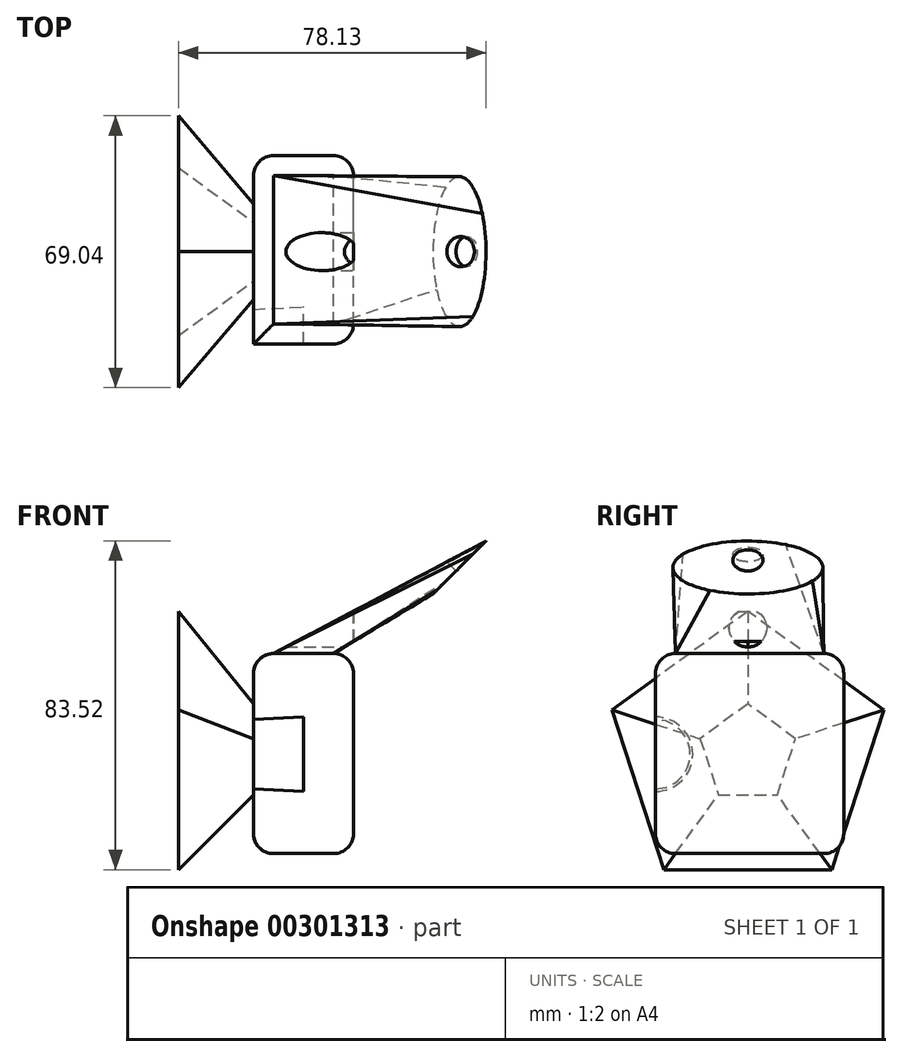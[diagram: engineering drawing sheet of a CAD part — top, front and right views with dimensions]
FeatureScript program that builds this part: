
annotation { "Feature Type Name" : "Feature", "Feature Type Description" : "" }
export const myFeature = defineFeature(function(context is Context, id is Id, definition is map)
    precondition{}
    {
        {
            var Q0;
            Q0=qCreatedBy(makeId("Right.planeOp"),FACE);
            var sketch = newSketch(context, id + "F0", { "sketchPlane" : qUnion([Q0])});
            skLineSegment(sketch, "E0.bottom", {"start": v(-23.46, 25.57) * mm, "end": v(24.36, 25.57) * mm});
            skLineSegment(sketch, "E0.top", {"start": v(-23.46, -25.27) * mm, "end": v(24.36, -25.27) * mm});
            skLineSegment(sketch, "E0.left", {"start": v(-23.46, 25.57) * mm, "end": v(-23.46, -25.27) * mm});
            skLineSegment(sketch, "E0.right", {"start": v(24.36, 25.57) * mm, "end": v(24.36, -25.27) * mm});
            skSolve(sketch);
        }
        {
            var Q0;
            Q0=makeQuery(id+"F0.imprint","IMPRINT",FACE,{"disambiguationData":[TD([[makeQuery(id+"F0.imprint","IMPRINT",EDGE,{"derivedFrom":sQuery(id+"F0.wireOp",EDGE,"E0.bottom")}),-1.0]])]});
            extrude(context, id + "F1", {"entities" : qUnion([Q0]), "depth" : 25.4 * mm});
        }
        {
            var Q0;
            Q0=makeQuery(id+"F1.opExtrude","SWEPT_EDGE",EDGE,{"disambiguationData":[OSD([sQuery(id+"F0.wireOp",EDGE,"E0.bottom"),sQuery(id+"F0.wireOp",EDGE,"E0.left")])]});
            var Q1;
            Q1=makeQuery(id+"F1.opExtrude","SWEPT_EDGE",EDGE,{"disambiguationData":[OSD([sQuery(id+"F0.wireOp",EDGE,"E0.bottom"),sQuery(id+"F0.wireOp",EDGE,"E0.right")])]});
            var Q2;
            Q2=makeQuery(id+"F1.opExtrude","SWEPT_FACE",FACE,{"disambiguationData":[OSD([sQuery(id+"F0.wireOp",EDGE,"E0.bottom")])]});
            var Q3;
            Q3=makeQuery(id+"F1.opExtrude","CAP_FACE",FACE,{"disambiguationData":[OSD([sQuery(id+"F0.wireOp",EDGE,"E0.bottom"),sQuery(id+"F0.wireOp",EDGE,"E0.top"),sQuery(id+"F0.wireOp",EDGE,"E0.left"),sQuery(id+"F0.wireOp",EDGE,"E0.right")])],"isStart":false});
            var Q4;
            Q4=makeQuery(id+"F1.opExtrude","CAP_EDGE",EDGE,{"disambiguationData":[OSD([sQuery(id+"F0.wireOp",EDGE,"E0.right")])],"isStart":true});
            var Q5;
            Q5=makeQuery(id+"F1.opExtrude","SWEPT_EDGE",EDGE,{"disambiguationData":[OSD([sQuery(id+"F0.wireOp",EDGE,"E0.top"),sQuery(id+"F0.wireOp",EDGE,"E0.right")])]});
            var Q6;
            Q6=makeQuery(id+"F1.opExtrude","CAP_EDGE",EDGE,{"disambiguationData":[OSD([sQuery(id+"F0.wireOp",EDGE,"E0.top")])],"isStart":true});
            var Q7;
            Q7=makeQuery(id+"F1.opExtrude","SWEPT_EDGE",EDGE,{"disambiguationData":[OSD([sQuery(id+"F0.wireOp",EDGE,"E0.top"),sQuery(id+"F0.wireOp",EDGE,"E0.left")])]});
            fillet(context, id + "F2", {"entities" : qUnion([Q0, Q1, Q2, Q3, Q4, Q5, Q6, Q7]), "radius" : 5.08 * mm, "tangentPropagation" : true, "allowEdgeOverflow" : false});
        }
        {
            var Q0;
            {var subQ0=sQuery(id+"F0.wireOp",EDGE,"E0.bottom");Q0=makeQuery(id+"F2.opFillet","BLEND_EDGE",EDGE,{"blendedFrom":[makeQuery(id+"F1.opExtrude","CAP_EDGE",EDGE,{"disambiguationData":[OSD([subQ0])],"isStart":false}),makeQuery(id+"F1.opExtrude","CAP_FACE",FACE,{"disambiguationData":[OSD([subQ0,sQuery(id+"F0.wireOp",EDGE,"E0.top"),sQuery(id+"F0.wireOp",EDGE,"E0.left"),sQuery(id+"F0.wireOp",EDGE,"E0.right")])],"isStart":false})],"blendedInto":[makeQuery(id+"F1.opExtrude","CAP_FACE",FACE,{"disambiguationData":[OSD([subQ0,sQuery(id+"F0.wireOp",EDGE,"E0.top"),sQuery(id+"F0.wireOp",EDGE,"E0.left"),sQuery(id+"F0.wireOp",EDGE,"E0.right")])],"isStart":false})]});}
            var Q1;
            Q1=makeQuery(id+"F1.opExtrude","CAP_FACE",FACE,{"disambiguationData":[OSD([sQuery(id+"F0.wireOp",EDGE,"E0.bottom"),sQuery(id+"F0.wireOp",EDGE,"E0.top"),sQuery(id+"F0.wireOp",EDGE,"E0.left"),sQuery(id+"F0.wireOp",EDGE,"E0.right")])],"isStart":false});
            cPlane(context, id + "F3", {"entities" : qUnion([Q0, Q1]), "cplaneType" : CPlaneType.LINE_ANGLE, "offset" : 25.4 * mm, "angle" : 45 * degree, "width" : 152.4 * mm, "height" : 152.4 * mm});
        }
        {
            var Q0;
            Q0=qCreatedBy(id+"F3.planeOp",FACE);
            var sketch = newSketch(context, id + "F4", { "sketchPlane" : qUnion([Q0])});
            skEllipse(sketch, "E1", {"center": v(0, 70.55) * mm, "majorRadius": 19.05 * mm, "minorRadius": 9.53 * mm, "majorAxis": v(1, 0)});
            skSolve(sketch);
        }
        {
            var Q1;
            Q1=makeQuery(id+"F1.opExtrude","SWEPT_FACE",FACE,{"disambiguationData":[OSD([sQuery(id+"F0.wireOp",EDGE,"E0.bottom")])]});
            var Q2;
            Q2=makeQuery(id+"F4.imprint","IMPRINT",FACE,{"disambiguationData":[TD([[makeQuery(id+"F4.imprint","IMPRINT",EDGE,{"derivedFrom":sQuery(id+"F4.wireOp",EDGE,"E1")}),1.0]])]});
            loft(context, id + "F5", {"operationType" : NewBodyOperationType.ADD, "sheetProfilesArray" : [{ "sheetProfileEntities" : qUnion([Q1]) }, { "sheetProfileEntities" : qUnion([Q2]) }]});
        }
        {
            var Q0;
            Q0=makeQuery(id+"F1.opExtrude","CAP_FACE",FACE,{"disambiguationData":[OSD([sQuery(id+"F0.wireOp",EDGE,"E0.bottom"),sQuery(id+"F0.wireOp",EDGE,"E0.top"),sQuery(id+"F0.wireOp",EDGE,"E0.left"),sQuery(id+"F0.wireOp",EDGE,"E0.right")])],"isStart":false});
            var sketch = newSketch(context, id + "F6", { "sketchPlane" : qUnion([Q0])});
            skCircle(sketch, "E2", {"center": v(0, 32.05) * mm, "radius": 4.81 * mm});
            skSolve(sketch);
        }
        {
            var Q0;
            Q0 = qSketchRegion(id + "F6", true);
            extrude(context, id + "F7", {"entities" : qUnion([Q0]), "operationType" : NewBodyOperationType.REMOVE, "endBound" : BoundingType.THROUGH_ALL, "oppositeDirection" : true, "depth" : 25.4 * mm});
        }
        {
            var Q0;
            Q0=makeQuery(id+"F1.opExtrude","CAP_FACE",FACE,{"disambiguationData":[OSD([sQuery(id+"F0.wireOp",EDGE,"E0.bottom"),sQuery(id+"F0.wireOp",EDGE,"E0.top"),sQuery(id+"F0.wireOp",EDGE,"E0.left"),sQuery(id+"F0.wireOp",EDGE,"E0.right")])],"isStart":true});
            var sketch = newSketch(context, id + "F8", { "sketchPlane" : qUnion([Q0])});
            skCircle(sketch, "E3", {"center": v(23.46, 0) * mm, "radius": 8.79 * mm});
            skSolve(sketch);
        }
        {
            var Q0;
            {var subQ0=sQuery(id+"F8.wireOp",EDGE,"E3");var subQ1=makeQuery(id+"F1.opExtrude","CAP_EDGE",EDGE,{"disambiguationData":[OSD([sQuery(id+"F0.wireOp",EDGE,"E0.left")])],"isStart":true});var subQ2=makeQuery(id+"F8.imprint","INTERSECT",VERTEX,{"disambiguationData":[OD(0.0)],"derivedFrom":[subQ1,subQ0]});Q0=makeQuery(id+"F8.imprint","IMPRINT",FACE,{"disambiguationData":[TD([[makeQuery(id+"F8.imprint","IMPRINT",EDGE,{"disambiguationData":[TD([[subQ2,-1.0]])],"derivedFrom":subQ0}),1.0]])]});}
            extrude(context, id + "F9", {"entities" : qUnion([Q0]), "operationType" : NewBodyOperationType.REMOVE, "oppositeDirection" : true, "depth" : 12.7 * mm, "hasDraft" : true, "draftAngle" : 3 * degree});
        }
        {
            var Q0;
            Q0=makeQuery(id+"F1.opExtrude","CAP_FACE",FACE,{"disambiguationData":[OSD([sQuery(id+"F0.wireOp",EDGE,"E0.bottom"),sQuery(id+"F0.wireOp",EDGE,"E0.top"),sQuery(id+"F0.wireOp",EDGE,"E0.left"),sQuery(id+"F0.wireOp",EDGE,"E0.right")])],"isStart":true});
            var sketch = newSketch(context, id + "F10", { "sketchPlane" : qUnion([Q0])});
            skCircle(sketch, "E4.cCircle", {"center": v(0, 0) * mm, "radius": 10.31 * mm, "construction": true});
            skLineSegment(sketch, "E4.0", {"start": v(12.13, 3.94) * mm, "end": v(7.5, -10.31) * mm});
            skLineSegment(sketch, "E4.1", {"start": v(7.5, -10.31) * mm, "end": v(-7.5, -10.31) * mm});
            skLineSegment(sketch, "E4.2", {"start": v(-7.5, -10.31) * mm, "end": v(-12.13, 3.94) * mm});
            skLineSegment(sketch, "E4.3", {"start": v(-12.13, 3.94) * mm, "end": v(0, 12.75) * mm});
            skLineSegment(sketch, "E4.4", {"start": v(0, 12.75) * mm, "end": v(12.13, 3.94) * mm});
            skPoint(sketch, "E4.0.midPoint", {"position": v(9.8, -3.19) * mm});
            skLineSegment(sketch, "E5.0", {"start": v(23.46, 20.49) * mm, "end": v(23.46, 8.79) * mm});
            skSolve(sketch);
        }
        {
            var Q0;
            Q0=makeQuery(id+"F10.imprint","IMPRINT",FACE,{"disambiguationData":[TD([[makeQuery(id+"F10.imprint","IMPRINT",EDGE,{"derivedFrom":sQuery(id+"F10.wireOp",EDGE,"E4.0")}),-1.0]])]});
            extrude(context, id + "F11", {"entities" : qUnion([Q0]), "operationType" : NewBodyOperationType.ADD, "depth" : 19.05 * mm, "hasDraft" : true, "draftAngle" : 45 * degree});
        }
        {
            var Q0;
            Q0=makeQuery(id+"F5.opLoft","CAP_FACE",FACE,{"disambiguationData":[OSD([makeQuery(id+"F4.imprint","IMPRINT",FACE,{"disambiguationData":[TD([[makeQuery(id+"F4.imprint","IMPRINT",EDGE,{"derivedFrom":sQuery(id+"F4.wireOp",EDGE,"E1")}),1.0]])]})])],"isStart":true});
            var sketch = newSketch(context, id + "F12", { "sketchPlane" : qUnion([Q0])});
            skCircle(sketch, "E6", {"center": v(0, 73.11) * mm, "radius": 3.81 * mm});
            skSolve(sketch);
        }
        {
            var Q0;
            Q0=makeQuery(id+"F12.imprint","IMPRINT",FACE,{"disambiguationData":[TD([[makeQuery(id+"F12.imprint","IMPRINT",EDGE,{"derivedFrom":sQuery(id+"F12.wireOp",EDGE,"E6")}),1.0]])]});
            extrude(context, id + "F13", {"entities" : qUnion([Q0]), "operationType" : NewBodyOperationType.REMOVE, "oppositeDirection" : true, "depth" : 25.4 * mm});
        }
    });
